# Revit family: Gira_206800
name_source: partatom
category: Electrical Fixtures
revit_build: Autodesk Revit 2017 (Build: 20160225_1515(x64)
units: mm (PartAtom-declared; Revit-internal decimal feet)

## family parameters
Cut with Voids When Loaded = No
Host = Face
Maintain Annotation Orientation = Yes
Part Type = Normal
Room Calculation Point = No
Round Connector Dimension = Use Diameter
Shared = No

## types (1)
- Gira_206800
    Andere Bussysteme = ohne
    Ausführung der Oberfläche = nicht zutreffend
    Available = Yes
    BIM (1) = https://media.live.bim.site Client.rfa?public/gira/9fde4c0/GiraHomeServer_GC19 Client.rfa
    Bussystem Funkbus = Nein
    Bussystem KNX = Ja
    Bussystem KNX-Funk = Nein
    Bussystem LON = Nein
    Bussystem Powernet = Nein
    Category = Bussystem-Mehrfach Bediengerät
    Data sheet (1) = https://katalog.gira.de
    Default Elevation = 1219 mm
    Description = Gira Control 19 Client 2   Der Gira Control 19 Client ist eine Anzeige- und Bedieneinheit zum Anschluss an den Gira HomeServer oder den Gira FacilityServer. Das Gerät ist PC-basiert und verfügt über einen TFT-Touchscreen mit 47 cm (19) Bilddiagonale.  Merkmale: - Visualisierung und Bedienung von Funktionen in der Gebäudesystemtechnik in Verbindung mit dem Gira HomeServer und oder dem Gira FacilityServer. - Anzeige von e-mails. - Wiedergabe von akustischen Signalen. - Als Wohnungsstation (mittels TKS-IP-Gateway) in Türkommunikationsanlagen geeignet. Gerätemerkmale: - PC mit Touchscreen. - Integriertes Netzteil. - Integrierter Lautsprecher. - Integriertes Mikrofon.  Software: Betriebssystem Microsoft(r) Windows(r) embedded Standard 7.:   Hinweise : - Kann auch in bestehende Gira Pro-face ServerClient 15 Gerätedosen verbaut werden. - Nur zur Verwendung im Innenbereich geeignet. - Anwendungsbereiche:    - Betrieb in stationärer Umgebung..   - Betrieb nur unter Umgebungsbedingungen die den Spezifikationen hinsichtlich Temperatur, Feuchte, Staub, Vibration usw. entsprechen.. - Der Gira AppShop ist der Marktplatz für interessante Lösungen und Anwendungen der intelligenten Gebäudetechnik. Inzwischen sind dort mehr als 200 Apps erhältlich, darunter Anwendungsbeschreibungen, Plug-ins, Funktionsvorlagen, Logikbausteine und Musterprojekte. Entdecken Sie jetzt Anwendungen für den Gira Control 19 Client 2.   www.appshop.gira.de.
    Funk bidirektional = Nein
    GTIN = 4010337022367
    HAN = 206800
    HeinzeBIM = https://bimportal.heinze.de
    Kategorie = Bussystem-Mehrfach Bediengerät
    Keynote = GiraHomeServer_GC19 Client
    Manufacturer = Gira
    Manufacturer URL = https://www.gira.de
    Mit Busankopplung = Ja
    Mit Display = Ja
    Montageart = unter Putz
    Name = Gira Control 19 Client 2 Elektronik
    Oberfläche = sonstige
    Region = DE
    Schutzart (IP) = IP20
    Transparent = Nein
    URL = http://katalog.gira.de
    Verfügbar = Ja
    Werkstoff = sonstige
    Werkstoffgüte = sonstige
    Zentrale Funktionseinheit für Sender/Aktoren = Ja

## geometry (parser evidence)
native form markers: Blend x4, Sweep x5
no freeform markers — native parametric forms only
